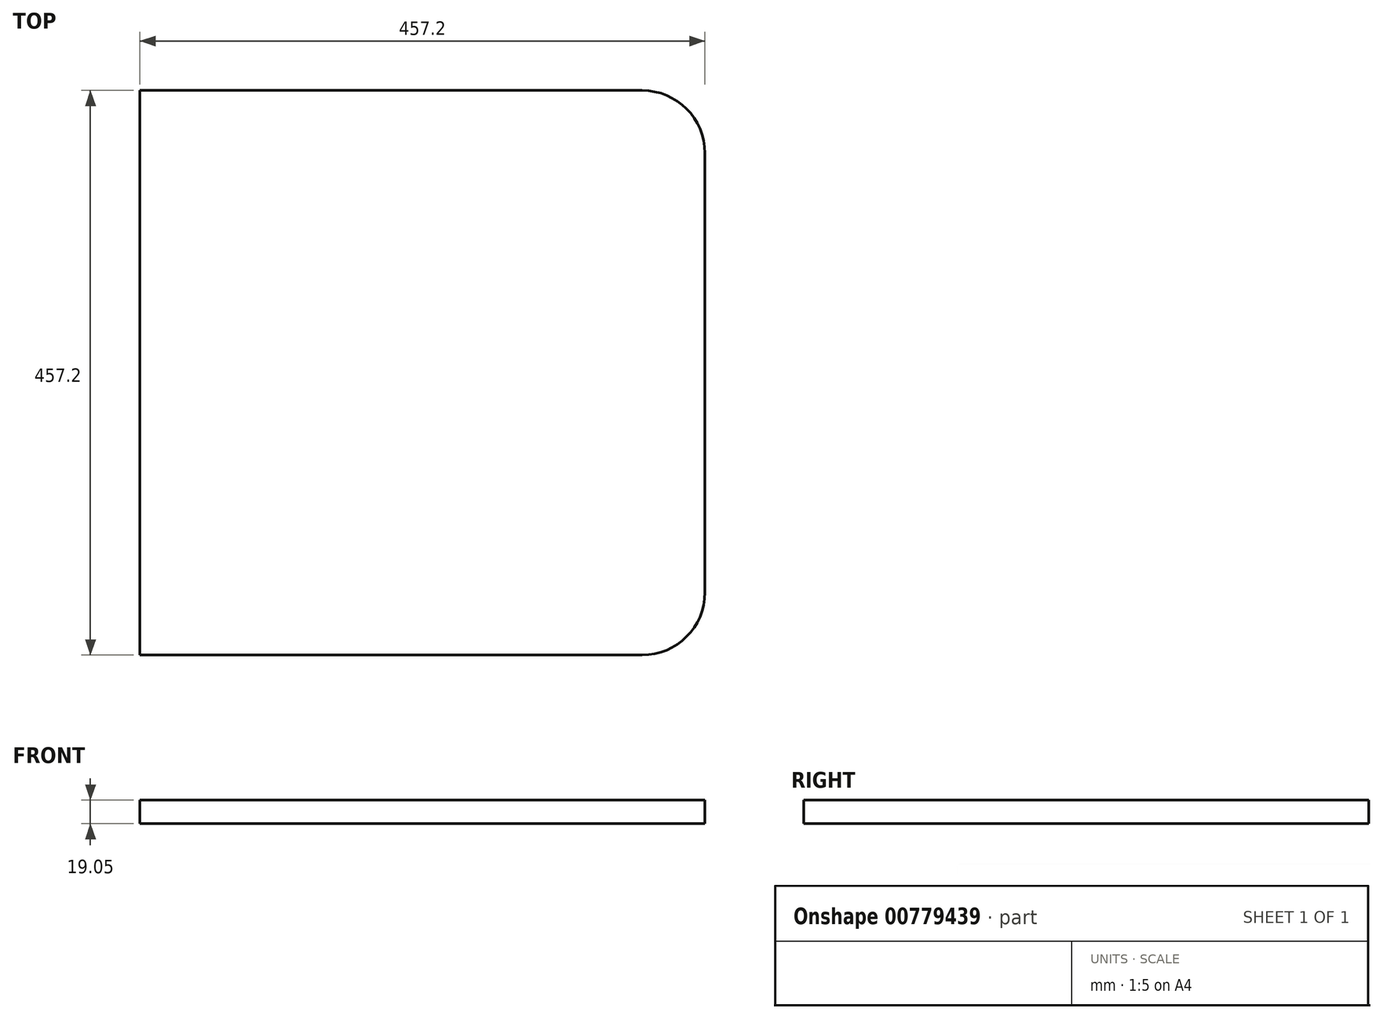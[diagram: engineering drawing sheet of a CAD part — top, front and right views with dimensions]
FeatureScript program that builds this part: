
annotation { "Feature Type Name" : "Feature", "Feature Type Description" : "" }
export const myFeature = defineFeature(function(context is Context, id is Id, definition is map)
    precondition{}
    {
        {
            var Q0;
            Q0=qCreatedBy(makeId("Top.planeOp"),FACE);
            var sketch = newSketch(context, id + "F0", { "sketchPlane" : qUnion([Q0])});
            skLineSegment(sketch, "E0.bottom", {"start": v(177.8, 228.6) * mm, "end": v(-228.6, 228.6) * mm});
            skLineSegment(sketch, "E0.top", {"start": v(177.8, -228.6) * mm, "end": v(-228.6, -228.6) * mm});
            skLineSegment(sketch, "E0.left", {"start": v(228.6, 177.8) * mm, "end": v(228.6, -177.8) * mm});
            skLineSegment(sketch, "E0.right", {"start": v(-228.6, 228.6) * mm, "end": v(-228.6, -228.6) * mm});
            skPoint(sketch, "E0.middle", {"position": v(0, 0) * mm});
            skPoint(sketch, "E1.visualSharp", {"position": v(228.6, 228.6) * mm});
            skArc(sketch, "E1.filletArc", {"start": v(228.6, 177.8) * mm, "mid": v(213.72, 213.72) * mm, "end": v(177.8, 228.6) * mm});
            skPoint(sketch, "E2.visualSharp", {"position": v(228.6, -228.6) * mm});
            skArc(sketch, "E2.filletArc", {"start": v(177.8, -228.6) * mm, "mid": v(213.72, -213.72) * mm, "end": v(228.6, -177.8) * mm});
            skSolve(sketch);
        }
        {
            var Q0;
            Q0=makeQuery(id+"F0.imprint","IMPRINT",FACE,{"disambiguationData":[TD([[makeQuery(id+"F0.imprint","IMPRINT",EDGE,{"derivedFrom":sQuery(id+"F0.wireOp",EDGE,"E0.bottom")}),1.0]])]});
            extrude(context, id + "F1", {"entities" : qUnion([Q0]), "depth" : 19.05 * mm, "offsetDistance" : 25.4 * mm});
        }
    });
